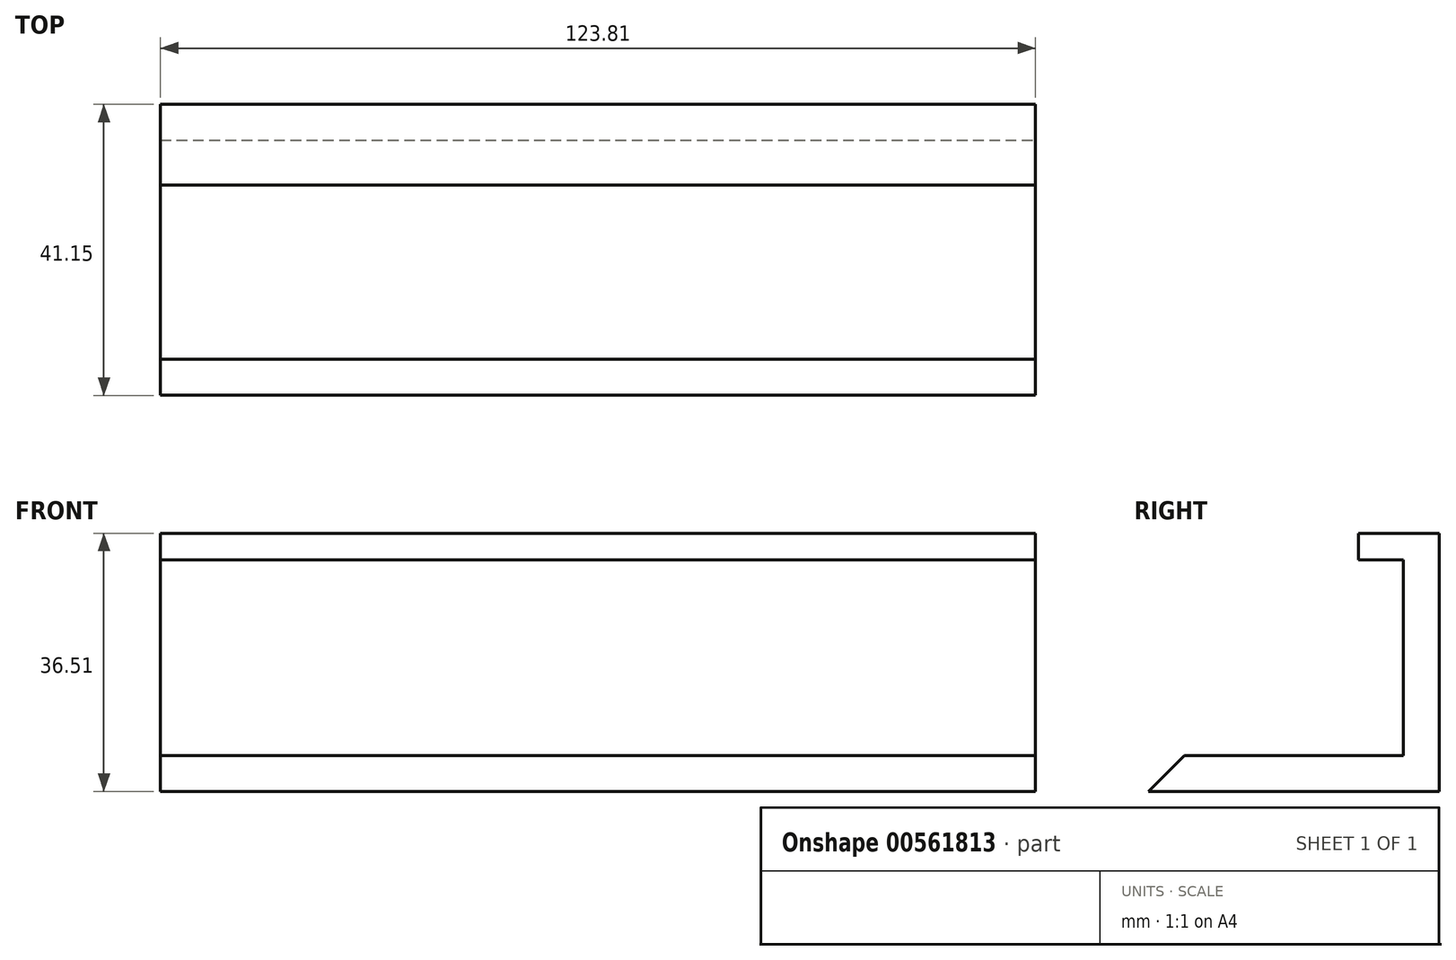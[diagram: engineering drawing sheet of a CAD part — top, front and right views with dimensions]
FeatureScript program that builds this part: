
annotation { "Feature Type Name" : "Feature", "Feature Type Description" : "" }
export const myFeature = defineFeature(function(context is Context, id is Id, definition is map)
    precondition{}
    {
        {
            var Q0;
            Q0=qCreatedBy(makeId("Front.planeOp"),FACE);
            var sketch = newSketch(context, id + "F0", { "sketchPlane" : qUnion([Q0])});
            skLineSegment(sketch, "E0.bottom", {"start": v(-57.2, 27.08) * mm, "end": v(66.62, 27.08) * mm});
            skLineSegment(sketch, "E0.top", {"start": v(-57.2, -9.43) * mm, "end": v(66.62, -9.43) * mm});
            skLineSegment(sketch, "E0.left", {"start": v(-57.2, 27.08) * mm, "end": v(-57.2, -9.43) * mm});
            skLineSegment(sketch, "E0.right", {"start": v(66.62, 27.08) * mm, "end": v(66.62, -9.43) * mm});
            skSolve(sketch);
        }
        {
            var Q0;
            Q0 = qSketchRegion(id + "F0", true);
            extrude(context, id + "F1", {"entities" : qUnion([Q0]), "depth" : 5.08 * mm, "offsetDistance" : 25.4 * mm});
        }
        {
            var Q0;
            Q0 = qSketchRegion(id + "F0", true);
            extrude(context, id + "F2", {"entities" : qUnion([Q0]), "operationType" : NewBodyOperationType.ADD, "depth" : 4.83 * mm, "offsetDistance" : 25.4 * mm});
        }
        {
            var Q0;
            Q0=makeQuery(id+"F1.opExtrude","CAP_FACE",FACE,{"disambiguationData":[OSD([sQuery(id+"F0.wireOp",EDGE,"E0.bottom"),sQuery(id+"F0.wireOp",EDGE,"E0.top"),sQuery(id+"F0.wireOp",EDGE,"E0.left"),sQuery(id+"F0.wireOp",EDGE,"E0.right")])],"isStart":false});
            var sketch = newSketch(context, id + "F3", { "sketchPlane" : qUnion([Q0])});
            skLineSegment(sketch, "E1.bottom", {"start": v(66.62, 27.08) * mm, "end": v(-57.2, 27.08) * mm});
            skLineSegment(sketch, "E1.top", {"start": v(66.62, 23.28) * mm, "end": v(-57.2, 23.28) * mm});
            skLineSegment(sketch, "E1.left", {"start": v(66.62, 27.08) * mm, "end": v(66.62, 23.28) * mm});
            skLineSegment(sketch, "E1.right", {"start": v(-57.2, 27.08) * mm, "end": v(-57.2, 23.28) * mm});
            skSolve(sketch);
        }
        {
            var Q0;
            Q0 = qSketchRegion(id + "F3", true);
            extrude(context, id + "F4", {"entities" : qUnion([Q0]), "operationType" : NewBodyOperationType.ADD, "depth" : 6.35 * mm, "offsetDistance" : 25.4 * mm});
        }
        {
            var Q0;
            Q0=makeQuery(id+"F1.opExtrude","CAP_FACE",FACE,{"disambiguationData":[OSD([sQuery(id+"F0.wireOp",EDGE,"E0.bottom"),sQuery(id+"F0.wireOp",EDGE,"E0.top"),sQuery(id+"F0.wireOp",EDGE,"E0.left"),sQuery(id+"F0.wireOp",EDGE,"E0.right")])],"isStart":false});
            var sketch = newSketch(context, id + "F5", { "sketchPlane" : qUnion([Q0])});
            skLineSegment(sketch, "E2.bottom", {"start": v(-57.2, -9.43) * mm, "end": v(66.62, -9.43) * mm});
            skLineSegment(sketch, "E2.top", {"start": v(-57.2, -4.35) * mm, "end": v(66.62, -4.35) * mm});
            skLineSegment(sketch, "E2.left", {"start": v(-57.2, -9.43) * mm, "end": v(-57.2, -4.35) * mm});
            skLineSegment(sketch, "E2.right", {"start": v(66.62, -9.43) * mm, "end": v(66.62, -4.35) * mm});
            skSolve(sketch);
        }
        {
            var Q0;
            Q0 = qSketchRegion(id + "F5", true);
            extrude(context, id + "F6", {"entities" : qUnion([Q0]), "operationType" : NewBodyOperationType.ADD, "depth" : 36.07 * mm, "offsetDistance" : 25.4 * mm});
        }
        {
            var Q0;
            Q0=makeQuery(id+"F6.opExtrude","CAP_EDGE",EDGE,{"disambiguationData":[OSD([sQuery(id+"F5.wireOp",EDGE,"E2.top")])],"isStart":false});
            chamfer(context, id + "F7", {"entities" : qUnion([Q0]), "width" : 5.08 * mm, "tangentPropagation" : true});
        }
    });
